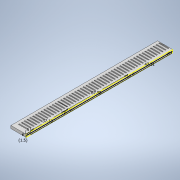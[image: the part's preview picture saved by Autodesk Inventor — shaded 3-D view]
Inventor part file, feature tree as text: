
AUTODESK INVENTOR PART (.ipt)
format: ipt  version: 2022.1 (Build 261234000, 234)  size: 427,520 bytes
history: native  units: mm
features: sketch x6, extrude x5, projected_geometry x1
ambient origin geometry x8: Origin, YZ Plane, XZ Plane, XY Plane, X Axis, Y Axis, Z Axis, Center Point
bodies: Solid1 (feature_tree)
feature tree (12):
  extrude  "Extrusion1"  Depth=16.0mm
  extrude  "Extrusion2"  Depth=10.0mm
  extrude  "Extrusion3"  Depth=3.0mm TaperAngle=0.0deg
  extrude  "Extrusion4"  Depth=3.02mm
  sketch  "Sketch5"  dims[d15=3.0mm d16=0.0mm d17=5.0mm]
  extrude  "Extrusion5"  Depth=5.0mm
  sketch  "Sketch1"  dims[d0=16.0mm d1=150.0mm]
  sketch  "Sketch2"  dims[d2=10.0mm d3=144.0mm]
  projected_geometry  "Projected Loop1"
  sketch  "Sketch3"  dims[d4=3.0mm d5=3.0mm d6=0.0mm]
  sketch  "Sketch4"  dims[d7=2.0mm d8=480.0mm d10=3.02mm d11=10.0mm d13=10.0mm]
  sketch  "Sketch6"  dims[d18=1.5mm d19=2.0mm d20=37.13mm d21=1.5mm d22=67.55mm d23=1.5mm d24=8.0mm d25=16.0mm d26=0.0mm d27=10.0mm d28=1.02mm d29=40.0mm d31=3.1mm d32=10.0mm d34=10.0mm d36=16.0mm d37=0.0mm d38=5.0mm d39=1.5mm d40=37.13mm d41=67.55mm d42=47.31mm d43=5.0mm d45=37.13mm d47=67.55mm d49=47.31mm d51=2.0mm d52=2.0mm d53=2.0mm d54=2.0mm d55=16.0mm d56=0.0mm]
